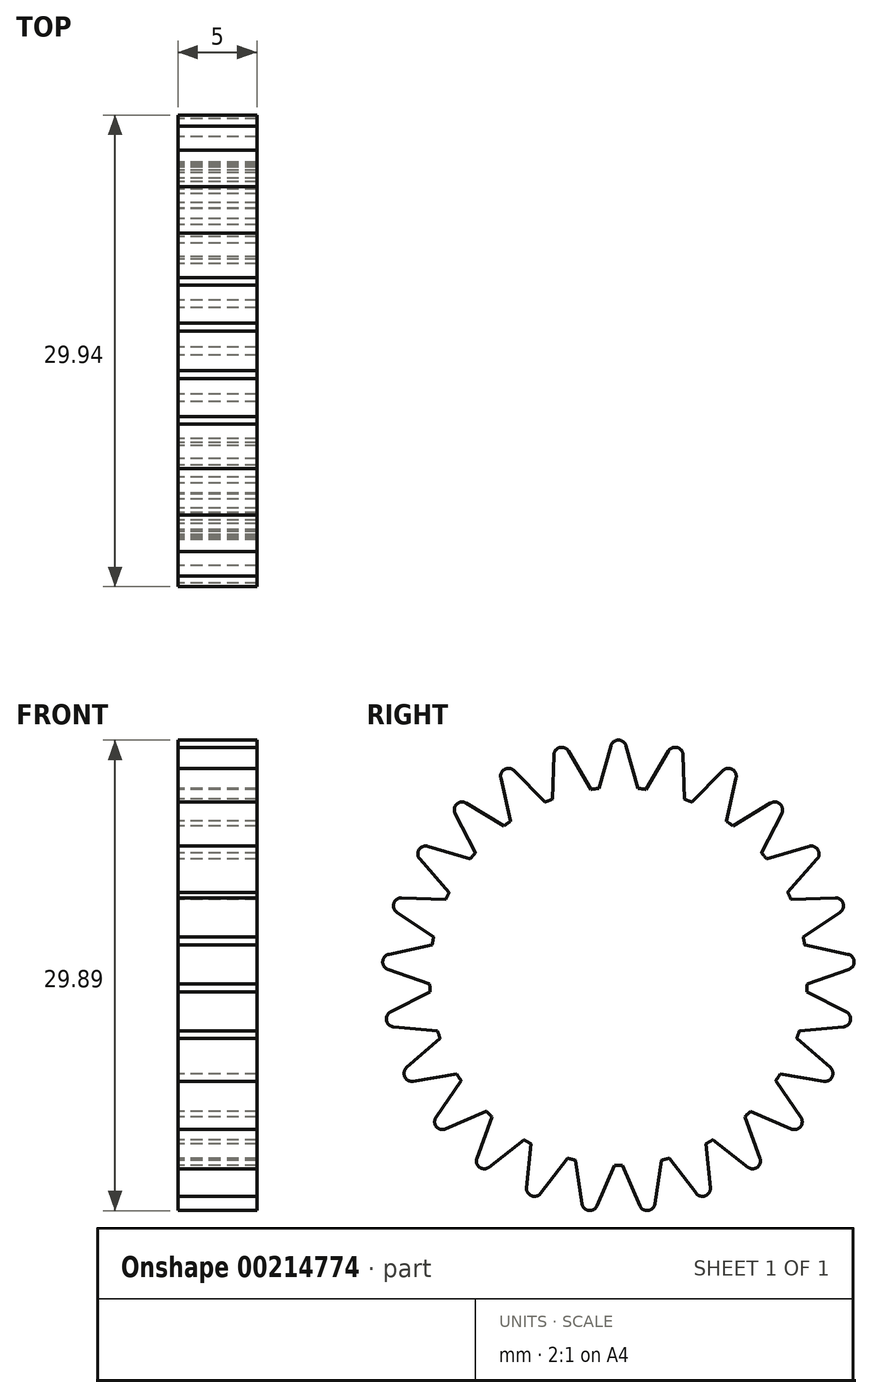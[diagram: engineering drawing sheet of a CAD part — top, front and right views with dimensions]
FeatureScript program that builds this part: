
annotation { "Feature Type Name" : "Feature", "Feature Type Description" : "" }
export const myFeature = defineFeature(function(context is Context, id is Id, definition is map)
    precondition{}
    {
        {
            var Q0;
            Q0=qCreatedBy(makeId("Right.planeOp"),FACE);
            var sketch = newSketch(context, id + "F0", { "sketchPlane" : qUnion([Q0])});
            skArc(sketch, "E0", {"start": v(0.48, 14.64) * mm, "mid": v(0, 15) * mm, "end": v(-0.48, 14.64) * mm});
            skLineSegment(sketch, "E1", {"start": v(-0.48, 14.64) * mm, "end": v(-1.25, 11.93) * mm});
            skLineSegment(sketch, "E2.MirrorCS", {"start": v(0.48, 14.64) * mm, "end": v(1.25, 11.93) * mm});
            skCircle(sketch, "E3", {"center": v(0, 0) * mm, "radius": 12 * mm});
            skLineSegment(sketch, "E4", {"start": v(0, 0) * mm, "end": v(0, 9.86) * mm, "construction": true});
            skLineSegment(sketch, "E5.1.0", {"start": v(-4.1, 14.06) * mm, "end": v(-4.18, 11.25) * mm});
            skArc(sketch, "E5.1.1", {"start": v(-3.17, 14.3) * mm, "mid": v(-3.73, 14.53) * mm, "end": v(-4.1, 14.06) * mm});
            skLineSegment(sketch, "E5.1.2", {"start": v(-3.17, 14.3) * mm, "end": v(-1.76, 11.87) * mm});
            skLineSegment(sketch, "E5.2.0", {"start": v(-7.47, 12.6) * mm, "end": v(-6.85, 9.86) * mm});
            skArc(sketch, "E5.2.1", {"start": v(-6.63, 13.06) * mm, "mid": v(-7.23, 13.14) * mm, "end": v(-7.47, 12.6) * mm});
            skLineSegment(sketch, "E5.2.2", {"start": v(-6.63, 13.06) * mm, "end": v(-4.65, 11.06) * mm});
            skLineSegment(sketch, "E5.3.0", {"start": v(-10.37, 10.34) * mm, "end": v(-9.08, 7.84) * mm});
            skArc(sketch, "E5.3.1", {"start": v(-9.67, 11) * mm, "mid": v(-10.27, 10.93) * mm, "end": v(-10.37, 10.34) * mm});
            skLineSegment(sketch, "E5.3.2", {"start": v(-9.67, 11) * mm, "end": v(-7.26, 9.56) * mm});
            skArc(sketch, "E5.3.3", {"start": v(-9.08, 7.84) * mm, "mid": v(8.21, -8.75) * mm, "end": v(-7.26, 9.56) * mm});
            skLineSegment(sketch, "E5.4.0", {"start": v(-12.62, 7.44) * mm, "end": v(-10.75, 5.34) * mm});
            skArc(sketch, "E5.4.1", {"start": v(-12.1, 8.25) * mm, "mid": v(-12.66, 8.04) * mm, "end": v(-12.62, 7.44) * mm});
            skLineSegment(sketch, "E5.4.2", {"start": v(-12.1, 8.25) * mm, "end": v(-9.4, 7.45) * mm});
            skLineSegment(sketch, "E5.5.0", {"start": v(-14.07, 4.07) * mm, "end": v(-11.74, 2.5) * mm});
            skArc(sketch, "E5.5.1", {"start": v(-13.77, 4.98) * mm, "mid": v(-14.27, 4.64) * mm, "end": v(-14.07, 4.07) * mm});
            skLineSegment(sketch, "E5.5.2", {"start": v(-13.77, 4.98) * mm, "end": v(-10.96, 4.88) * mm});
            skLineSegment(sketch, "E5.6.0", {"start": v(-14.64, 0.44) * mm, "end": v(-11.99, -0.5) * mm});
            skArc(sketch, "E5.6.1", {"start": v(-14.58, 1.4) * mm, "mid": v(-14.97, 0.94) * mm, "end": v(-14.64, 0.44) * mm});
            skLineSegment(sketch, "E5.6.2", {"start": v(-14.58, 1.4) * mm, "end": v(-11.83, 2) * mm});
            skLineSegment(sketch, "E5.7.0", {"start": v(-14.29, -3.22) * mm, "end": v(-11.49, -3.47) * mm});
            skArc(sketch, "E5.7.1", {"start": v(-14.47, -2.27) * mm, "mid": v(-14.73, -2.81) * mm, "end": v(-14.29, -3.22) * mm});
            skLineSegment(sketch, "E5.7.2", {"start": v(-14.47, -2.27) * mm, "end": v(-11.96, -1) * mm});
            skLineSegment(sketch, "E5.8.0", {"start": v(-13.04, -6.67) * mm, "end": v(-10.27, -6.21) * mm});
            skArc(sketch, "E5.8.1", {"start": v(-13.45, -5.8) * mm, "mid": v(-13.57, -6.39) * mm, "end": v(-13.04, -6.67) * mm});
            skLineSegment(sketch, "E5.8.2", {"start": v(-13.45, -5.8) * mm, "end": v(-11.33, -3.95) * mm});
            skLineSegment(sketch, "E5.9.0", {"start": v(-10.97, -9.7) * mm, "end": v(-8.4, -8.57) * mm});
            skArc(sketch, "E5.9.1", {"start": v(-11.58, -8.96) * mm, "mid": v(-11.56, -9.56) * mm, "end": v(-10.97, -9.7) * mm});
            skLineSegment(sketch, "E5.9.2", {"start": v(-11.58, -8.96) * mm, "end": v(-10, -6.64) * mm});
            skLineSegment(sketch, "E5.10.0", {"start": v(-8.21, -12.12) * mm, "end": v(-6, -10.4) * mm});
            skArc(sketch, "E5.10.1", {"start": v(-9, -11.56) * mm, "mid": v(-8.82, -12.14) * mm, "end": v(-8.21, -12.12) * mm});
            skLineSegment(sketch, "E5.10.2", {"start": v(-9, -11.56) * mm, "end": v(-8.03, -8.92) * mm});
            skLineSegment(sketch, "E5.11.0", {"start": v(-4.94, -13.79) * mm, "end": v(-3.23, -11.56) * mm});
            skArc(sketch, "E5.11.1", {"start": v(-5.84, -13.43) * mm, "mid": v(-5.52, -13.95) * mm, "end": v(-4.94, -13.79) * mm});
            skLineSegment(sketch, "E5.11.2", {"start": v(-5.84, -13.43) * mm, "end": v(-5.56, -10.64) * mm});
            skArc(sketch, "E5.11.3", {"start": v(-9.08, 7.84) * mm, "mid": v(8.21, -8.75) * mm, "end": v(-7.26, 9.56) * mm});
            skLineSegment(sketch, "E5.12.0", {"start": v(-1.36, -14.58) * mm, "end": v(-0.25, -12) * mm});
            skArc(sketch, "E5.12.1", {"start": v(-2.31, -14.46) * mm, "mid": v(-1.88, -14.88) * mm, "end": v(-1.36, -14.58) * mm});
            skLineSegment(sketch, "E5.12.2", {"start": v(-2.31, -14.46) * mm, "end": v(-2.74, -11.68) * mm});
            skLineSegment(sketch, "E5.13.0", {"start": v(2.31, -14.46) * mm, "end": v(2.74, -11.68) * mm});
            skArc(sketch, "E5.13.1", {"start": v(1.36, -14.58) * mm, "mid": v(1.88, -14.88) * mm, "end": v(2.31, -14.46) * mm});
            skLineSegment(sketch, "E5.13.2", {"start": v(1.36, -14.58) * mm, "end": v(0.25, -12) * mm});
            skLineSegment(sketch, "E5.14.0", {"start": v(5.84, -13.43) * mm, "end": v(5.56, -10.64) * mm});
            skArc(sketch, "E5.14.1", {"start": v(4.94, -13.79) * mm, "mid": v(5.52, -13.95) * mm, "end": v(5.84, -13.43) * mm});
            skLineSegment(sketch, "E5.14.2", {"start": v(4.94, -13.79) * mm, "end": v(3.23, -11.56) * mm});
            skLineSegment(sketch, "E5.15.0", {"start": v(9, -11.56) * mm, "end": v(8.03, -8.92) * mm});
            skArc(sketch, "E5.15.1", {"start": v(8.21, -12.12) * mm, "mid": v(8.82, -12.14) * mm, "end": v(9, -11.56) * mm});
            skLineSegment(sketch, "E5.15.2", {"start": v(8.21, -12.12) * mm, "end": v(6, -10.4) * mm});
            skArc(sketch, "E5.15.3", {"start": v(-9.08, 7.84) * mm, "mid": v(8.21, -8.75) * mm, "end": v(-7.26, 9.56) * mm});
            skLineSegment(sketch, "E5.16.0", {"start": v(11.58, -8.96) * mm, "end": v(10, -6.64) * mm});
            skArc(sketch, "E5.16.1", {"start": v(10.97, -9.7) * mm, "mid": v(11.56, -9.56) * mm, "end": v(11.58, -8.96) * mm});
            skLineSegment(sketch, "E5.16.2", {"start": v(10.97, -9.7) * mm, "end": v(8.4, -8.57) * mm});
            skLineSegment(sketch, "E5.17.0", {"start": v(13.45, -5.8) * mm, "end": v(11.33, -3.95) * mm});
            skArc(sketch, "E5.17.1", {"start": v(13.04, -6.67) * mm, "mid": v(13.57, -6.39) * mm, "end": v(13.45, -5.8) * mm});
            skLineSegment(sketch, "E5.17.2", {"start": v(13.04, -6.67) * mm, "end": v(10.27, -6.21) * mm});
            skLineSegment(sketch, "E5.18.0", {"start": v(14.47, -2.27) * mm, "end": v(11.96, -1) * mm});
            skArc(sketch, "E5.18.1", {"start": v(14.29, -3.22) * mm, "mid": v(14.73, -2.81) * mm, "end": v(14.47, -2.27) * mm});
            skLineSegment(sketch, "E5.18.2", {"start": v(14.29, -3.22) * mm, "end": v(11.49, -3.47) * mm});
            skLineSegment(sketch, "E5.19.0", {"start": v(14.58, 1.4) * mm, "end": v(11.83, 2) * mm});
            skArc(sketch, "E5.19.1", {"start": v(14.64, 0.44) * mm, "mid": v(14.97, 0.94) * mm, "end": v(14.58, 1.4) * mm});
            skLineSegment(sketch, "E5.19.2", {"start": v(14.64, 0.44) * mm, "end": v(11.99, -0.5) * mm});
            skLineSegment(sketch, "E5.20.0", {"start": v(13.77, 4.98) * mm, "end": v(10.96, 4.88) * mm});
            skArc(sketch, "E5.20.1", {"start": v(14.07, 4.07) * mm, "mid": v(14.27, 4.64) * mm, "end": v(13.77, 4.98) * mm});
            skLineSegment(sketch, "E5.20.2", {"start": v(14.07, 4.07) * mm, "end": v(11.74, 2.5) * mm});
            skLineSegment(sketch, "E5.21.0", {"start": v(12.1, 8.25) * mm, "end": v(9.4, 7.45) * mm});
            skArc(sketch, "E5.21.1", {"start": v(12.62, 7.44) * mm, "mid": v(12.66, 8.04) * mm, "end": v(12.1, 8.25) * mm});
            skLineSegment(sketch, "E5.21.2", {"start": v(12.62, 7.44) * mm, "end": v(10.75, 5.34) * mm});
            skLineSegment(sketch, "E5.22.0", {"start": v(9.67, 11) * mm, "end": v(7.26, 9.56) * mm});
            skArc(sketch, "E5.22.1", {"start": v(10.37, 10.34) * mm, "mid": v(10.27, 10.93) * mm, "end": v(9.67, 11) * mm});
            skLineSegment(sketch, "E5.22.2", {"start": v(10.37, 10.34) * mm, "end": v(9.08, 7.84) * mm});
            skLineSegment(sketch, "E6.2.23.0", {"start": v(6.63, 13.06) * mm, "end": v(4.65, 11.06) * mm});
            skArc(sketch, "E6.3.23.0", {"start": v(7.47, 12.6) * mm, "mid": v(7.23, 13.14) * mm, "end": v(6.63, 13.06) * mm});
            skLineSegment(sketch, "E6.7.23.0", {"start": v(7.47, 12.6) * mm, "end": v(6.85, 9.86) * mm});
            skLineSegment(sketch, "E6.2.24.0", {"start": v(3.17, 14.3) * mm, "end": v(1.76, 11.87) * mm});
            skArc(sketch, "E6.3.24.0", {"start": v(4.1, 14.06) * mm, "mid": v(3.73, 14.53) * mm, "end": v(3.17, 14.3) * mm});
            skLineSegment(sketch, "E6.7.24.0", {"start": v(4.1, 14.06) * mm, "end": v(4.18, 11.25) * mm});
            skSolve(sketch);
        }
        {
            var Q0;
            Q0 = qSketchRegion(id + "F0", true);
            extrude(context, id + "F1", {"entities" : qUnion([Q0]), "depth" : 5 * mm});
        }
    });
